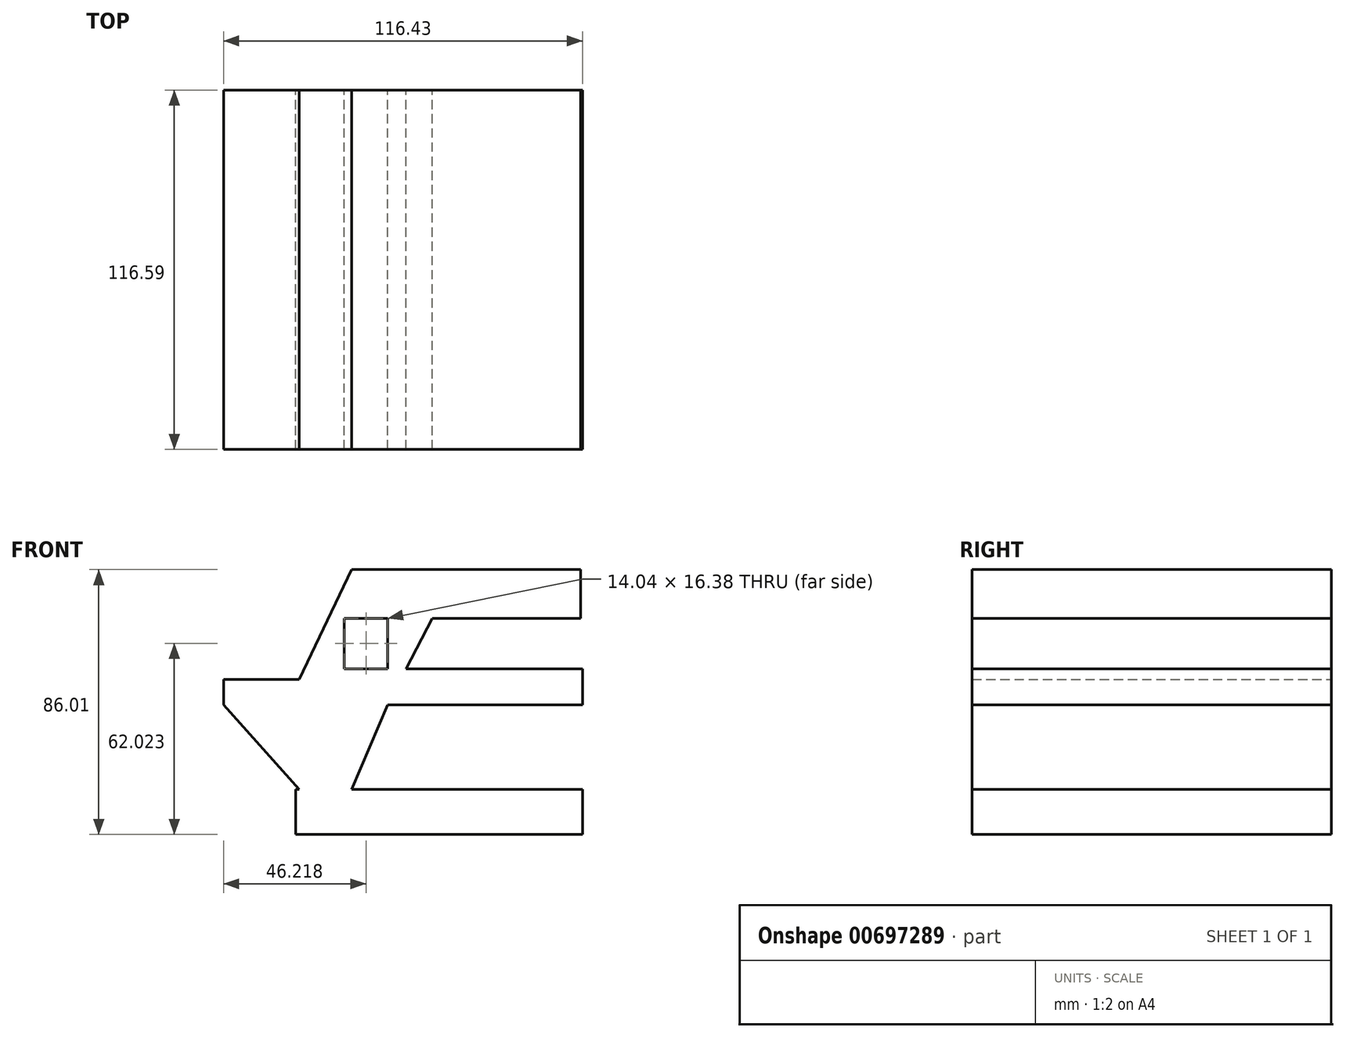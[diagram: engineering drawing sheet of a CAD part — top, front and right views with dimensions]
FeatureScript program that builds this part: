
annotation { "Feature Type Name" : "Feature", "Feature Type Description" : "" }
export const myFeature = defineFeature(function(context is Context, id is Id, definition is map)
    precondition{}
    {
        {
            var Q0;
            Q0=qCreatedBy(makeId("Front.planeOp"),FACE);
            var sketch = newSketch(context, id + "F0", { "sketchPlane" : qUnion([Q0])});
            skLineSegment(sketch, "E0.bottom", {"start": v(-67.72, 8.2) * mm, "end": v(-43.15, 8.2) * mm});
            skLineSegment(sketch, "E0.top", {"start": v(-67.72, 0) * mm, "end": v(-43.15, 0) * mm});
            skLineSegment(sketch, "E0.left", {"start": v(-67.72, 8.2) * mm, "end": v(-67.72, 0) * mm});
            skLineSegment(sketch, "E0.right", {"start": v(-43.15, 8.2) * mm, "end": v(-43.15, 0) * mm});
            skLineSegment(sketch, "E1", {"start": v(-43.15, 8.2) * mm, "end": v(-26.18, 43.88) * mm});
            skLineSegment(sketch, "E2", {"start": v(-26.18, 43.88) * mm, "end": v(48.12, 43.88) * mm});
            skLineSegment(sketch, "E3", {"start": v(48.12, 43.88) * mm, "end": v(48.12, 28.08) * mm});
            skLineSegment(sketch, "E4", {"start": v(48.12, 28.08) * mm, "end": v(0, 28.08) * mm});
            skLineSegment(sketch, "E5", {"start": v(0, 28.08) * mm, "end": v(-14.48, 0) * mm});
            skLineSegment(sketch, "E6", {"start": v(-14.48, 0) * mm, "end": v(-26.18, -27.5) * mm});
            skLineSegment(sketch, "E7", {"start": v(-26.18, -27.5) * mm, "end": v(-43.15, -27.5) * mm});
            skLineSegment(sketch, "E8", {"start": v(-43.15, -27.5) * mm, "end": v(-67.72, 0) * mm});
            skLineSegment(sketch, "E9.bottom", {"start": v(-28.52, 28.08) * mm, "end": v(-14.48, 28.08) * mm});
            skLineSegment(sketch, "E9.top", {"start": v(-28.52, 11.7) * mm, "end": v(-14.48, 11.7) * mm});
            skLineSegment(sketch, "E9.left", {"start": v(-28.52, 28.08) * mm, "end": v(-28.52, 11.7) * mm});
            skLineSegment(sketch, "E9.right", {"start": v(-14.48, 28.08) * mm, "end": v(-14.48, 11.7) * mm});
            skLineSegment(sketch, "E10.bottom", {"start": v(-12.14, 11.7) * mm, "end": v(48.7, 11.7) * mm});
            skLineSegment(sketch, "E10.top", {"start": v(-12.14, 0) * mm, "end": v(48.7, 0) * mm});
            skLineSegment(sketch, "E10.left", {"start": v(-12.14, 11.7) * mm, "end": v(-12.14, 0) * mm});
            skLineSegment(sketch, "E10.right", {"start": v(48.7, 11.7) * mm, "end": v(48.7, 0) * mm});
            skLineSegment(sketch, "E11.bottom", {"start": v(0, 0) * mm, "end": v(-28.52, 0) * mm});
            skLineSegment(sketch, "E11.top", {"start": v(0, 11.7) * mm, "end": v(-28.52, 11.7) * mm});
            skLineSegment(sketch, "E11.left", {"start": v(0, 0) * mm, "end": v(0, 11.7) * mm});
            skLineSegment(sketch, "E11.right", {"start": v(-28.52, 0) * mm, "end": v(-28.52, 11.7) * mm});
            skLineSegment(sketch, "E12.bottom", {"start": v(-26.18, -27.5) * mm, "end": v(-44.32, -27.5) * mm});
            skLineSegment(sketch, "E12.top", {"start": v(-26.18, -42.13) * mm, "end": v(-44.32, -42.13) * mm});
            skLineSegment(sketch, "E12.left", {"start": v(-26.18, -27.5) * mm, "end": v(-26.18, -42.13) * mm});
            skLineSegment(sketch, "E12.right", {"start": v(-44.32, -27.5) * mm, "end": v(-44.32, -42.13) * mm});
            skLineSegment(sketch, "E13.bottom", {"start": v(-26.18, -42.13) * mm, "end": v(48.7, -42.13) * mm});
            skLineSegment(sketch, "E13.top", {"start": v(-26.18, -27.5) * mm, "end": v(48.7, -27.5) * mm});
            skLineSegment(sketch, "E13.left", {"start": v(-26.18, -42.13) * mm, "end": v(-26.18, -27.5) * mm});
            skLineSegment(sketch, "E13.right", {"start": v(48.7, -42.13) * mm, "end": v(48.7, -27.5) * mm});
            skSolve(sketch);
        }
        {
            var Q0;
            Q0 = qSketchRegion(id + "F0", true);
            extrude(context, id + "F1", {"entities" : qUnion([Q0]), "depth" : 25.4 * mm, "offsetDistance" : 25.4 * mm});
        }
        {
            var Q0;
            Q0=makeQuery(id+"F1.opExtrude","CAP_FACE",FACE,{"disambiguationData":[OSD([sQuery(id+"F0.wireOp",EDGE,"E0.bottom"),sQuery(id+"F0.wireOp",EDGE,"E0.left"),sQuery(id+"F0.wireOp",EDGE,"E1"),sQuery(id+"F0.wireOp",EDGE,"E2"),sQuery(id+"F0.wireOp",EDGE,"E3"),sQuery(id+"F0.wireOp",EDGE,"E4"),sQuery(id+"F0.wireOp",EDGE,"E5"),sQuery(id+"F0.wireOp",EDGE,"E6"),sQuery(id+"F0.wireOp",EDGE,"E8"),sQuery(id+"F0.wireOp",EDGE,"E9.bottom"),sQuery(id+"F0.wireOp",EDGE,"E9.left"),sQuery(id+"F0.wireOp",EDGE,"E9.right"),sQuery(id+"F0.wireOp",EDGE,"E10.bottom"),sQuery(id+"F0.wireOp",EDGE,"E10.top"),sQuery(id+"F0.wireOp",EDGE,"E10.right"),sQuery(id+"F0.wireOp",EDGE,"E11.bottom"),sQuery(id+"F0.wireOp",EDGE,"E11.top"),sQuery(id+"F0.wireOp",EDGE,"E12.bottom"),sQuery(id+"F0.wireOp",EDGE,"E12.top"),sQuery(id+"F0.wireOp",EDGE,"E12.right"),sQuery(id+"F0.wireOp",EDGE,"E13.bottom"),sQuery(id+"F0.wireOp",EDGE,"E13.top"),sQuery(id+"F0.wireOp",EDGE,"E13.right")])],"isStart":false});
            extrude(context, id + "F2", {"entities" : qUnion([Q0]), "operationType" : NewBodyOperationType.ADD, "depth" : 91.19 * mm, "offsetDistance" : 25.4 * mm});
        }
    });
